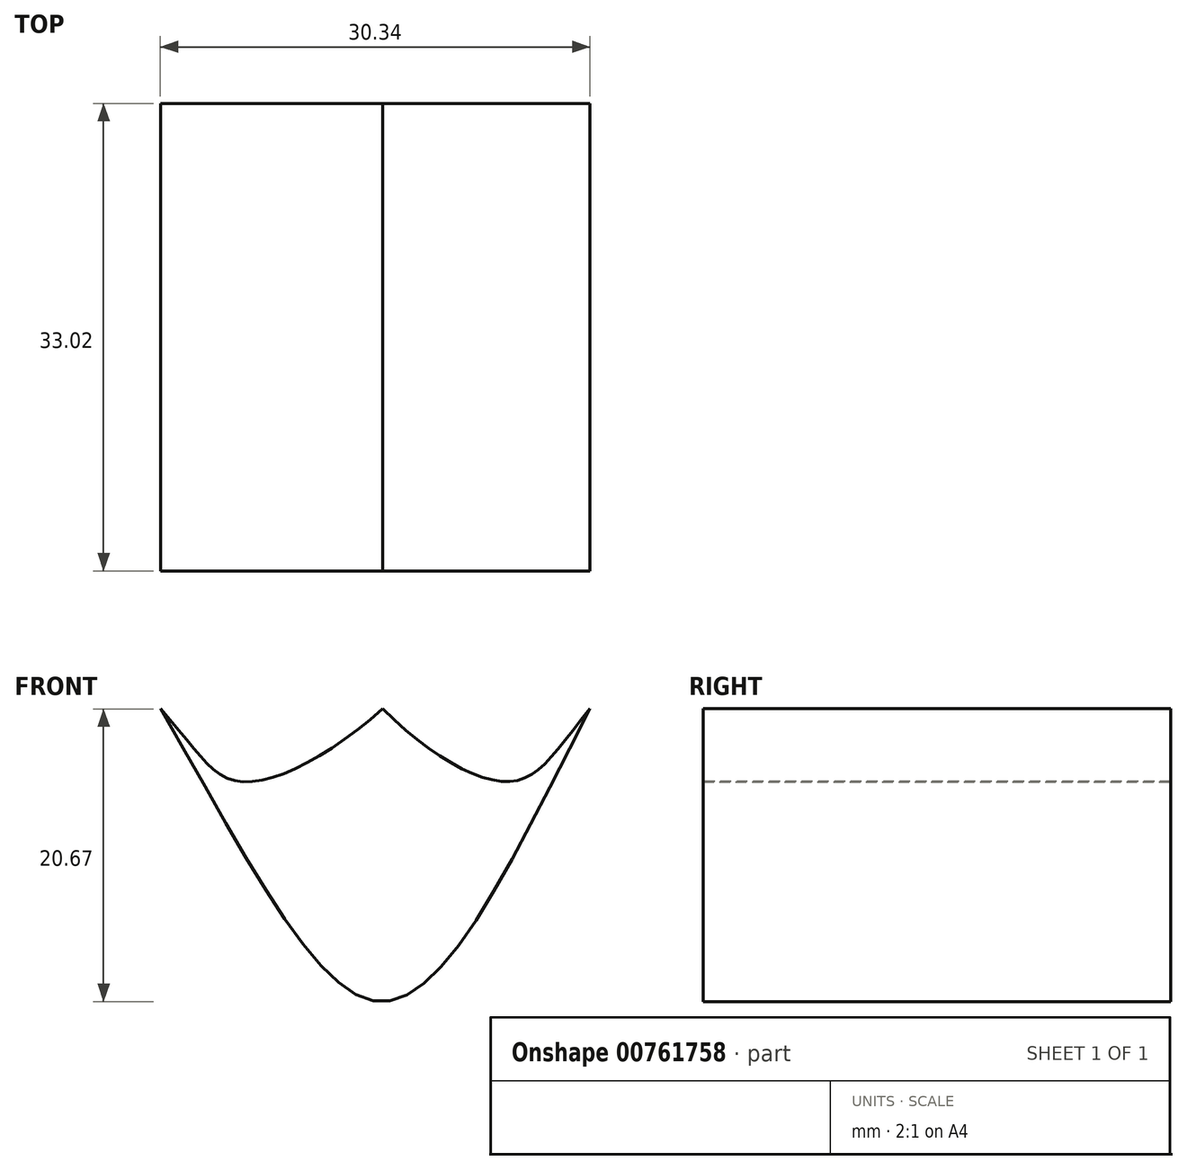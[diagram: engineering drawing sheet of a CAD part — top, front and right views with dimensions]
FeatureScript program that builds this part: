
annotation { "Feature Type Name" : "Feature", "Feature Type Description" : "" }
export const myFeature = defineFeature(function(context is Context, id is Id, definition is map)
    precondition{}
    {
        {
            var Q0;
            Q0=qCreatedBy(makeId("Front.planeOp"),FACE);
            var sketch = newSketch(context, id + "F0", { "sketchPlane" : qUnion([Q0])});
            skFitSpline(sketch, "E0", {"points": [v(0, 14.36) * mm, v(-10.34, 9.26) * mm, v(-15.7, 14.36) * mm], "startDerivative": vector(-20.5, -18.16) * mm, "endDerivative": vector(-16.77, 18.12) * mm});
            skFitSpline(sketch, "E1", {"points": [v(0, 14.36) * mm, v(9.26, 9.26) * mm, v(14.63, 14.36) * mm], "startDerivative": vector(18.53, -18.37) * mm, "endDerivative": vector(15.54, 18.72) * mm});
            skFitSpline(sketch, "E2", {"points": [v(-15.7, 14.36) * mm, v(0, -6.3) * mm, v(14.63, 14.36) * mm], "startDerivative": vector(37.73, -64.42) * mm, "endDerivative": vector(33.68, 65.27) * mm});
            skSolve(sketch);
        }
        {
            var Q0;
            Q0=makeQuery(id+"F0.imprint","IMPRINT",FACE,{"disambiguationData":[TD([[makeQuery(id+"F0.imprint","IMPRINT",EDGE,{"derivedFrom":sQuery(id+"F0.wireOp",EDGE,"E0")}),1.0]])]});
            extrude(context, id + "F1", {"entities" : qUnion([Q0]), "depth" : 33.02 * mm, "offsetDistance" : 25.4 * mm});
        }
    });
